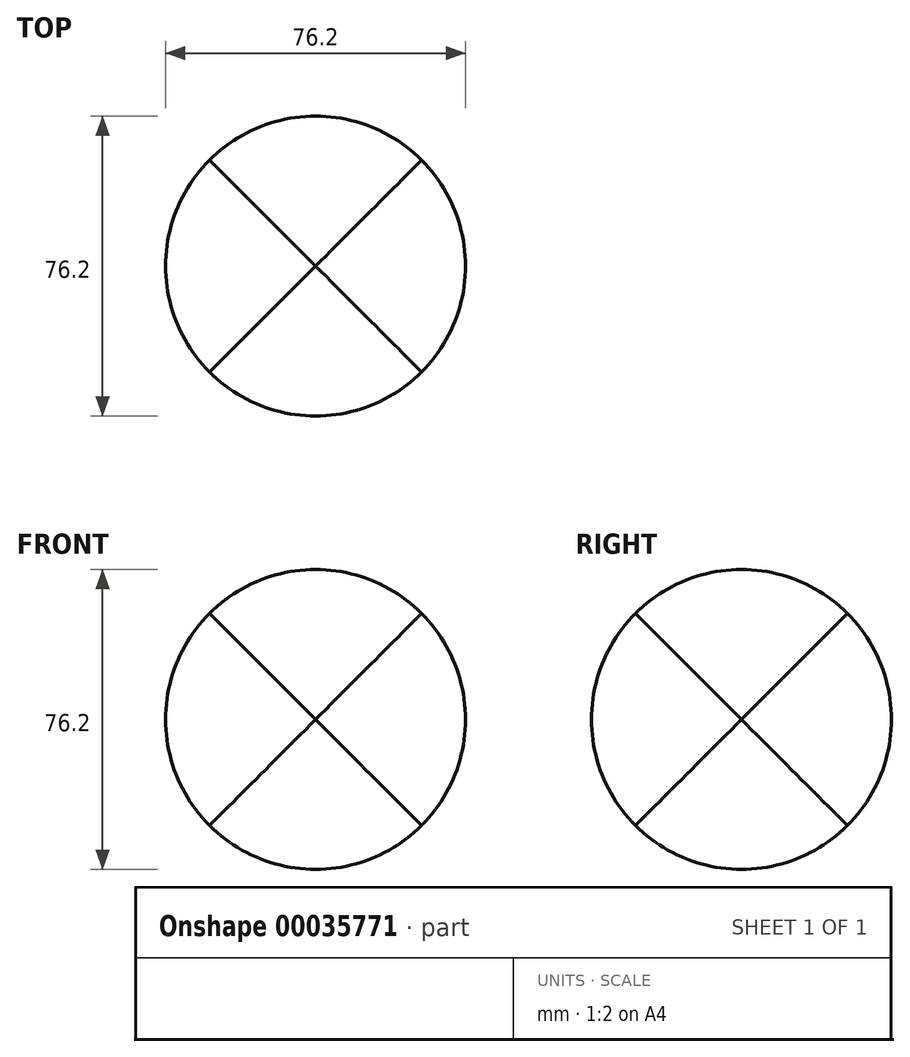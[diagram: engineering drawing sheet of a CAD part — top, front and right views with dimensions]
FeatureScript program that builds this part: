
annotation { "Feature Type Name" : "Feature", "Feature Type Description" : "" }
export const myFeature = defineFeature(function(context is Context, id is Id, definition is map)
    precondition{}
    {
        {
            var Q0;
            Q0=qCreatedBy(makeId("Front.planeOp"),FACE);
            var sketch = newSketch(context, id + "F0", { "sketchPlane" : qUnion([Q0])});
            skLineSegment(sketch, "E0.bottom", {"start": v(0, 0) * mm, "end": v(76.2, 0) * mm});
            skLineSegment(sketch, "E0.top", {"start": v(0, 76.2) * mm, "end": v(76.2, 76.2) * mm});
            skLineSegment(sketch, "E0.left", {"start": v(0, 0) * mm, "end": v(0, 76.2) * mm});
            skLineSegment(sketch, "E0.right", {"start": v(76.2, 0) * mm, "end": v(76.2, 76.2) * mm});
            skSolve(sketch);
        }
        {
            var Q0;
            Q0 = qSketchRegion(id + "F0", true);
            extrude(context, id + "F1", {"entities" : qUnion([Q0]), "depth" : 76.2 * mm});
        }
        {
            var Q0;
            Q0=makeQuery(id+"F1.opExtrude","SWEPT_FACE",FACE,{"disambiguationData":[OSD([sQuery(id+"F0.wireOp",EDGE,"E0.top")])]});
            var sketch = newSketch(context, id + "F2", { "sketchPlane" : qUnion([Q0])});
            skLineSegment(sketch, "E1", {"start": v(76.2, -38.1) * mm, "end": v(0, -38.1) * mm, "construction": true});
            skLineSegment(sketch, "E2", {"start": v(38.1, -76.2) * mm, "end": v(38.1, -38.1) * mm, "construction": true});
            skCircle(sketch, "E3", {"center": v(38.1, -38.1) * mm, "radius": 38.1 * mm});
            skSolve(sketch);
        }
        {
            var Q0;
            Q0=makeQuery(id+"F1.opExtrude","CAP_FACE",FACE,{"disambiguationData":[OSD([sQuery(id+"F0.wireOp",EDGE,"E0.bottom"),sQuery(id+"F0.wireOp",EDGE,"E0.top"),sQuery(id+"F0.wireOp",EDGE,"E0.left"),sQuery(id+"F0.wireOp",EDGE,"E0.right")])],"isStart":false});
            var sketch = newSketch(context, id + "F3", { "sketchPlane" : qUnion([Q0])});
            skLineSegment(sketch, "E4", {"start": v(0, 38.1) * mm, "end": v(76.2, 38.1) * mm, "construction": true});
            skLineSegment(sketch, "E5", {"start": v(38.1, 0) * mm, "end": v(38.1, 38.1) * mm, "construction": true});
            skCircle(sketch, "E6", {"center": v(38.1, 38.1) * mm, "radius": 38.1 * mm});
            skSolve(sketch);
        }
        {
            var Q0;
            Q0=makeQuery(id+"F1.opExtrude","SWEPT_FACE",FACE,{"disambiguationData":[OSD([sQuery(id+"F0.wireOp",EDGE,"E0.right")])]});
            var sketch = newSketch(context, id + "F4", { "sketchPlane" : qUnion([Q0])});
            skLineSegment(sketch, "E7", {"start": v(-38.1, 76.2) * mm, "end": v(-38.1, 0) * mm, "construction": true});
            skLineSegment(sketch, "E8", {"start": v(0, 38.1) * mm, "end": v(-38.1, 38.1) * mm, "construction": true});
            skCircle(sketch, "E9", {"center": v(-38.1, 38.1) * mm, "radius": 38.1 * mm});
            skSolve(sketch);
        }
        {
            var Q0;
            {var subQ0=sQuery(id+"F0.wireOp",EDGE,"E0.top");var subQ1=makeQuery(id+"F1.opExtrude","CAP_EDGE",EDGE,{"disambiguationData":[OSD([subQ0])],"isStart":false});var subQ2=sQuery(id+"F2.wireOp",EDGE,"E3");var subQ3=makeQuery(id+"F2.imprint","INTERSECT",VERTEX,{"derivedFrom":[subQ1,subQ2]});Q0=makeQuery(id+"F2.imprint","IMPRINT",FACE,{"disambiguationData":[TD([[makeQuery(id+"F2.imprint","IMPRINT",EDGE,{"disambiguationData":[TD([[subQ3,-1.0]])],"derivedFrom":subQ2}),-1.0]])]});}
            var Q1;
            {var subQ0=sQuery(id+"F0.wireOp",EDGE,"E0.top");var subQ1=makeQuery(id+"F1.opExtrude","CAP_EDGE",EDGE,{"disambiguationData":[OSD([subQ0])],"isStart":true});var subQ2=sQuery(id+"F2.wireOp",EDGE,"E3");var subQ3=makeQuery(id+"F2.imprint","INTERSECT",VERTEX,{"derivedFrom":[subQ1,subQ2]});Q1=makeQuery(id+"F2.imprint","IMPRINT",FACE,{"disambiguationData":[TD([[makeQuery(id+"F2.imprint","IMPRINT",EDGE,{"disambiguationData":[TD([[subQ3,1.0]])],"derivedFrom":subQ2}),-1.0]])]});}
            var Q2;
            {var subQ0=sQuery(id+"F0.wireOp",EDGE,"E0.top");var subQ1=makeQuery(id+"F1.opExtrude","CAP_EDGE",EDGE,{"disambiguationData":[OSD([subQ0])],"isStart":true});var subQ2=sQuery(id+"F2.wireOp",EDGE,"E3");var subQ3=makeQuery(id+"F2.imprint","INTERSECT",VERTEX,{"derivedFrom":[subQ1,subQ2]});Q2=makeQuery(id+"F2.imprint","IMPRINT",FACE,{"disambiguationData":[TD([[makeQuery(id+"F2.imprint","IMPRINT",EDGE,{"disambiguationData":[TD([[subQ3,-1.0]])],"derivedFrom":subQ2}),-1.0]])]});}
            var Q3;
            {var subQ0=sQuery(id+"F0.wireOp",EDGE,"E0.top");var subQ1=makeQuery(id+"F1.opExtrude","CAP_EDGE",EDGE,{"disambiguationData":[OSD([subQ0])],"isStart":false});var subQ2=sQuery(id+"F2.wireOp",EDGE,"E3");var subQ3=makeQuery(id+"F2.imprint","INTERSECT",VERTEX,{"derivedFrom":[subQ1,subQ2]});Q3=makeQuery(id+"F2.imprint","IMPRINT",FACE,{"disambiguationData":[TD([[makeQuery(id+"F2.imprint","IMPRINT",EDGE,{"disambiguationData":[TD([[subQ3,1.0]])],"derivedFrom":subQ2}),-1.0]])]});}
            extrude(context, id + "F5", {"entities" : qUnion([Q0, Q1, Q2, Q3]), "operationType" : NewBodyOperationType.REMOVE, "endBound" : BoundingType.THROUGH_ALL, "oppositeDirection" : true, "depth" : 25.4 * mm});
        }
        {
            var Q0;
            {var subQ1=sQuery(id+"F3.wireOp",EDGE,"E6");var subQ3=makeQuery(id+"F1.opExtrude","CAP_EDGE",EDGE,{"disambiguationData":[OSD([sQuery(id+"F0.wireOp",EDGE,"E0.top")])],"isStart":false});var subQ5=makeQuery(id+"F3.imprint","INTERSECT",VERTEX,{"derivedFrom":[subQ3,subQ1]});Q0=makeQuery(id+"F3.imprint","IMPRINT",FACE,{"disambiguationData":[TD([[makeQuery(id+"F3.imprint","IMPRINT",EDGE,{"disambiguationData":[TD([[subQ5,1.0]])],"derivedFrom":subQ1}),-1.0]])]});}
            var Q1;
            {var subQ1=sQuery(id+"F3.wireOp",EDGE,"E6");var subQ3=makeQuery(id+"F1.opExtrude","CAP_EDGE",EDGE,{"disambiguationData":[OSD([sQuery(id+"F0.wireOp",EDGE,"E0.top")])],"isStart":false});var subQ5=makeQuery(id+"F3.imprint","INTERSECT",VERTEX,{"derivedFrom":[subQ3,subQ1]});Q1=makeQuery(id+"F3.imprint","IMPRINT",FACE,{"disambiguationData":[TD([[makeQuery(id+"F3.imprint","IMPRINT",EDGE,{"disambiguationData":[TD([[subQ5,-1.0]])],"derivedFrom":subQ1}),-1.0]])]});}
            var Q2;
            {var subQ0=makeQuery(id+"F1.opExtrude","CAP_EDGE",EDGE,{"disambiguationData":[OSD([sQuery(id+"F0.wireOp",EDGE,"E0.right")])],"isStart":false});var subQ1=sQuery(id+"F3.wireOp",EDGE,"E6");var subQ2=makeQuery(id+"F3.imprint","INTERSECT",VERTEX,{"derivedFrom":[subQ0,subQ1]});Q2=makeQuery(id+"F3.imprint","IMPRINT",FACE,{"disambiguationData":[TD([[makeQuery(id+"F3.imprint","IMPRINT",EDGE,{"disambiguationData":[TD([[subQ2,1.0]])],"derivedFrom":subQ1}),-1.0]])]});}
            var Q3;
            {var subQ0=makeQuery(id+"F1.opExtrude","CAP_EDGE",EDGE,{"disambiguationData":[OSD([sQuery(id+"F0.wireOp",EDGE,"E0.left")])],"isStart":false});var subQ1=sQuery(id+"F3.wireOp",EDGE,"E6");var subQ2=makeQuery(id+"F3.imprint","INTERSECT",VERTEX,{"derivedFrom":[subQ0,subQ1]});Q3=makeQuery(id+"F3.imprint","IMPRINT",FACE,{"disambiguationData":[TD([[makeQuery(id+"F3.imprint","IMPRINT",EDGE,{"disambiguationData":[TD([[subQ2,-1.0]])],"derivedFrom":subQ1}),-1.0]])]});}
            extrude(context, id + "F6", {"entities" : qUnion([Q0, Q1, Q2, Q3]), "operationType" : NewBodyOperationType.REMOVE, "endBound" : BoundingType.THROUGH_ALL, "oppositeDirection" : true, "depth" : 25.4 * mm});
        }
        {
            var Q0;
            {var subQ0=sQuery(id+"F0.wireOp",EDGE,"E0.right");var subQ1=makeQuery(id+"F1.opExtrude","CAP_EDGE",EDGE,{"disambiguationData":[OSD([subQ0])],"isStart":true});var subQ2=sQuery(id+"F4.wireOp",EDGE,"E9");var subQ3=makeQuery(id+"F4.imprint","INTERSECT",VERTEX,{"derivedFrom":[subQ1,subQ2]});Q0=makeQuery(id+"F4.imprint","IMPRINT",FACE,{"disambiguationData":[TD([[makeQuery(id+"F4.imprint","IMPRINT",EDGE,{"disambiguationData":[TD([[subQ3,-1.0]])],"derivedFrom":subQ2}),-1.0]])]});}
            var Q1;
            {var subQ0=sQuery(id+"F0.wireOp",EDGE,"E0.right");var subQ1=makeQuery(id+"F1.opExtrude","CAP_EDGE",EDGE,{"disambiguationData":[OSD([subQ0])],"isStart":true});var subQ2=sQuery(id+"F4.wireOp",EDGE,"E9");var subQ3=makeQuery(id+"F4.imprint","INTERSECT",VERTEX,{"derivedFrom":[subQ1,subQ2]});Q1=makeQuery(id+"F4.imprint","IMPRINT",FACE,{"disambiguationData":[TD([[makeQuery(id+"F4.imprint","IMPRINT",EDGE,{"disambiguationData":[TD([[subQ3,1.0]])],"derivedFrom":subQ2}),-1.0]])]});}
            var Q2;
            {var subQ0=sQuery(id+"F0.wireOp",EDGE,"E0.right");var subQ1=makeQuery(id+"F1.opExtrude","CAP_EDGE",EDGE,{"disambiguationData":[OSD([subQ0])],"isStart":false});var subQ2=sQuery(id+"F4.wireOp",EDGE,"E9");var subQ3=makeQuery(id+"F4.imprint","INTERSECT",VERTEX,{"derivedFrom":[subQ1,subQ2]});Q2=makeQuery(id+"F4.imprint","IMPRINT",FACE,{"disambiguationData":[TD([[makeQuery(id+"F4.imprint","IMPRINT",EDGE,{"disambiguationData":[TD([[subQ3,-1.0]])],"derivedFrom":subQ2}),-1.0]])]});}
            var Q3;
            {var subQ0=sQuery(id+"F0.wireOp",EDGE,"E0.right");var subQ1=makeQuery(id+"F1.opExtrude","CAP_EDGE",EDGE,{"disambiguationData":[OSD([subQ0])],"isStart":false});var subQ2=sQuery(id+"F4.wireOp",EDGE,"E9");var subQ3=makeQuery(id+"F4.imprint","INTERSECT",VERTEX,{"derivedFrom":[subQ1,subQ2]});Q3=makeQuery(id+"F4.imprint","IMPRINT",FACE,{"disambiguationData":[TD([[makeQuery(id+"F4.imprint","IMPRINT",EDGE,{"disambiguationData":[TD([[subQ3,1.0]])],"derivedFrom":subQ2}),-1.0]])]});}
            extrude(context, id + "F7", {"entities" : qUnion([Q0, Q1, Q2, Q3]), "operationType" : NewBodyOperationType.REMOVE, "endBound" : BoundingType.THROUGH_ALL, "oppositeDirection" : true, "depth" : 25.4 * mm});
        }
    });
